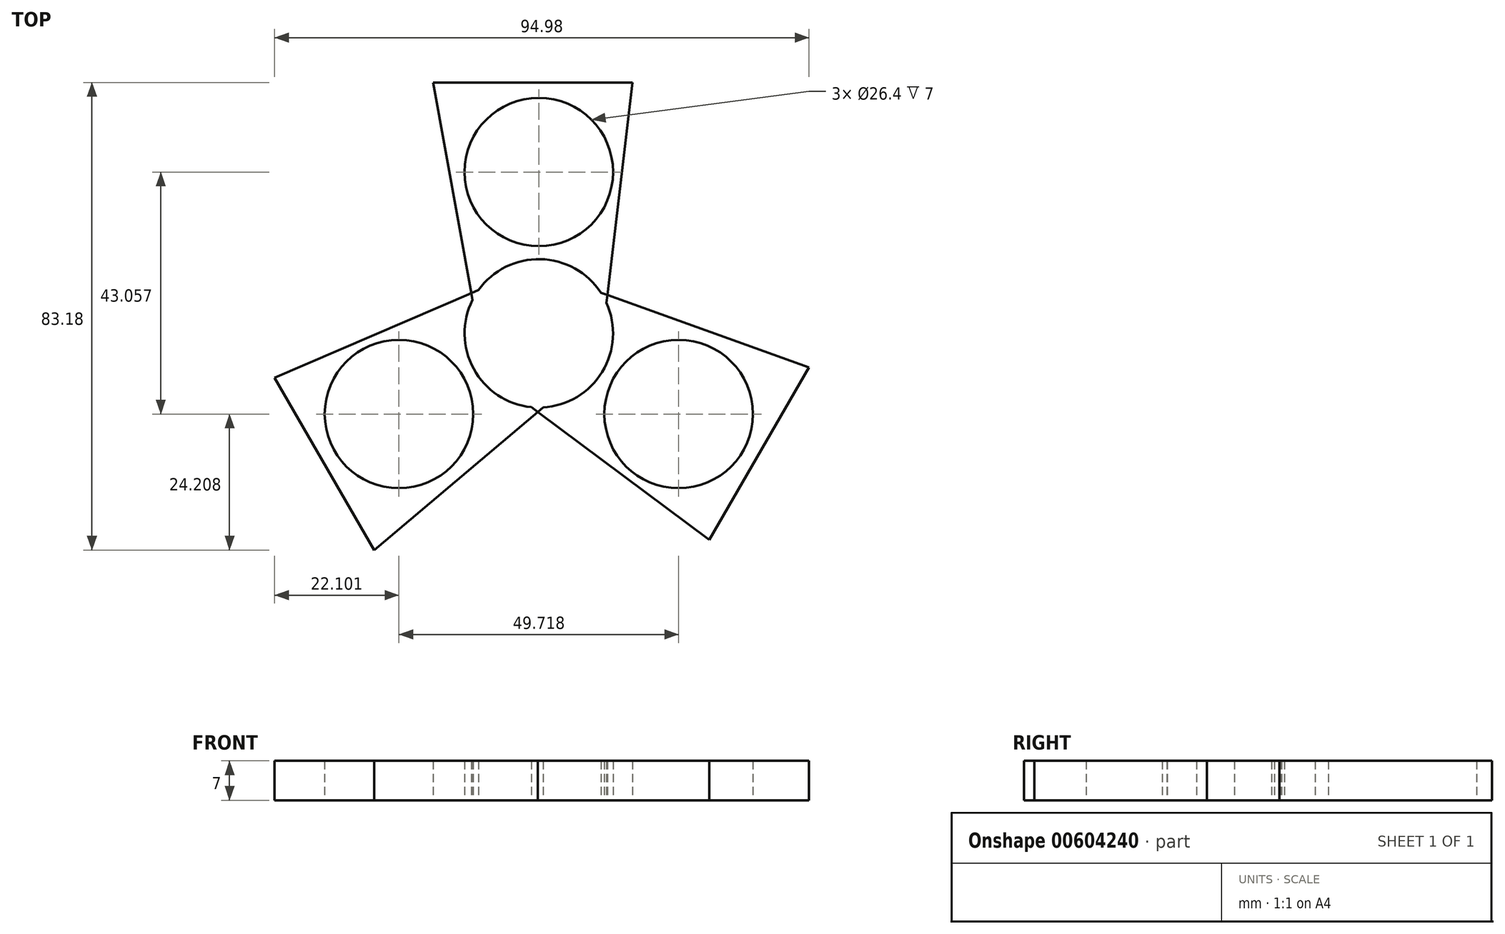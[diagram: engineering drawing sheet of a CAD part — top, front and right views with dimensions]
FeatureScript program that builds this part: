
annotation { "Feature Type Name" : "Feature", "Feature Type Description" : "" }
export const myFeature = defineFeature(function(context is Context, id is Id, definition is map)
    precondition{}
    {
        {
            var Q0;
            Q0=qCreatedBy(makeId("Top.planeOp"),FACE);
            var sketch = newSketch(context, id + "F0", { "sketchPlane" : qUnion([Q0])});
            skCircle(sketch, "E0", {"center": v(0, 0) * mm, "radius": 11.2 * mm});
            skCircle(sketch, "E1", {"center": v(0, 28.7) * mm, "radius": 11.2 * mm});
            skLineSegment(sketch, "E2", {"start": v(11.14, -71) * mm, "end": v(-13.2, -71) * mm});
            skCircle(sketch, "E3", {"center": v(0, 0) * mm, "radius": 13.2 * mm});
            skCircle(sketch, "E4", {"center": v(0, 28.7) * mm, "radius": 13.2 * mm});
            skCircle(sketch, "E5.1.0", {"center": v(-24.86, -14.35) * mm, "radius": 11.2 * mm});
            skCircle(sketch, "E5.1.1", {"center": v(-24.86, -14.35) * mm, "radius": 13.2 * mm});
            skCircle(sketch, "E5.2.0", {"center": v(24.86, -14.35) * mm, "radius": 11.2 * mm});
            skCircle(sketch, "E5.2.1", {"center": v(24.86, -14.35) * mm, "radius": 13.2 * mm});
            skLineSegment(sketch, "E6", {"start": v(0, 44.62) * mm, "end": v(-18.76, 44.62) * mm});
            skLineSegment(sketch, "E7", {"start": v(-18.76, 44.62) * mm, "end": v(0, 44.62) * mm});
            skLineSegment(sketch, "E8", {"start": v(16.64, 44.62) * mm, "end": v(0, 44.62) * mm});
            skLineSegment(sketch, "E9", {"start": v(16.64, 44.62) * mm, "end": v(12.04, 5.4) * mm});
            skLineSegment(sketch, "E10", {"start": v(-18.76, 44.62) * mm, "end": v(-11.79, 5.94) * mm});
            skLineSegment(sketch, "E11.1.0", {"start": v(-29.26, -38.56) * mm, "end": v(-38.64, -22.31) * mm});
            skLineSegment(sketch, "E11.1.1", {"start": v(-29.26, -38.56) * mm, "end": v(0.75, -13.18) * mm});
            skLineSegment(sketch, "E11.1.2", {"start": v(-46.96, -7.9) * mm, "end": v(-38.64, -22.31) * mm});
            skLineSegment(sketch, "E11.1.3", {"start": v(-46.96, -7.9) * mm, "end": v(-10.7, 7.73) * mm});
            skLineSegment(sketch, "E11.2.0", {"start": v(48.02, -6.06) * mm, "end": v(38.64, -22.31) * mm});
            skLineSegment(sketch, "E11.2.1", {"start": v(48.02, -6.06) * mm, "end": v(11.04, 7.24) * mm});
            skLineSegment(sketch, "E11.2.2", {"start": v(30.32, -36.72) * mm, "end": v(38.64, -22.31) * mm});
            skLineSegment(sketch, "E11.2.3", {"start": v(30.32, -36.72) * mm, "end": v(-1.34, -13.13) * mm});
            skSolve(sketch);
        }
        {
            var Q0;
            Q0=makeQuery(id+"F0.imprint","IMPRINT",FACE,{"disambiguationData":[TD([[makeQuery(id+"F0.imprint","IMPRINT",EDGE,{"derivedFrom":sQuery(id+"F0.wireOp",EDGE,"E5.1.1")}),-1.0]])]});
            var Q1;
            Q1=makeQuery(id+"F0.imprint","IMPRINT",FACE,{"disambiguationData":[TD([[makeQuery(id+"F0.imprint","IMPRINT",EDGE,{"derivedFrom":sQuery(id+"F0.wireOp",EDGE,"E5.2.1")}),-1.0]])]});
            var Q2;
            Q2=makeQuery(id+"F0.imprint","IMPRINT",FACE,{"disambiguationData":[TD([[makeQuery(id+"F0.imprint","IMPRINT",EDGE,{"derivedFrom":sQuery(id+"F0.wireOp",EDGE,"E4")}),-1.0]])]});
            extrude(context, id + "F1", {"entities" : qUnion([Q0, Q1, Q2]), "depth" : 7 * mm, "offsetDistance" : 25 * mm});
        }
    });
